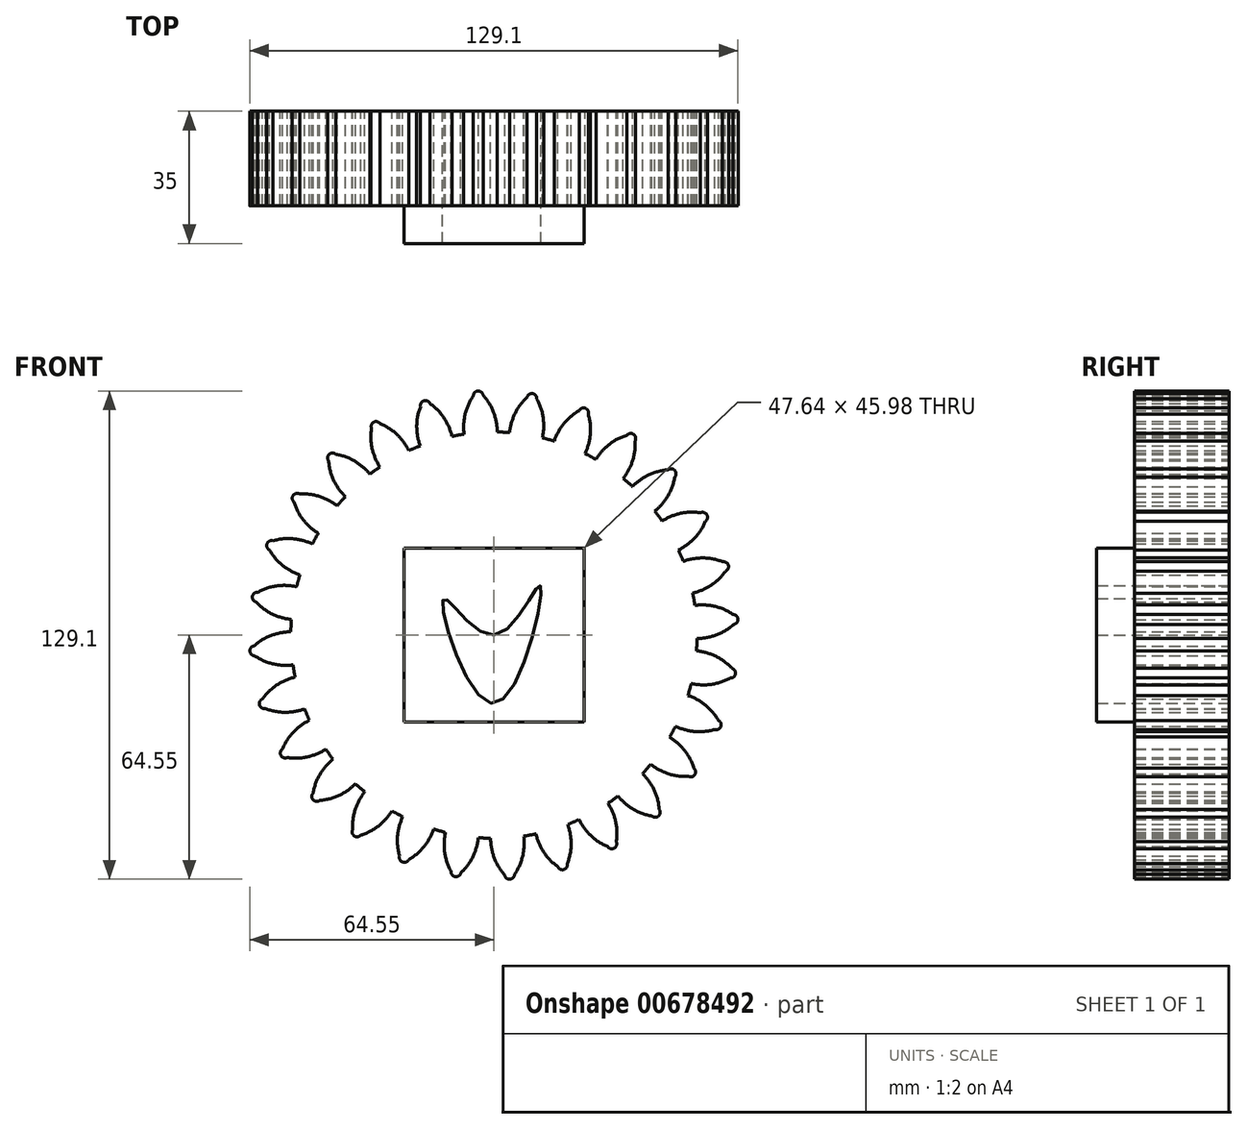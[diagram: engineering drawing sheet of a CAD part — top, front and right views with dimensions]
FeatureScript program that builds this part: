
annotation { "Feature Type Name" : "Feature", "Feature Type Description" : "" }
export const myFeature = defineFeature(function(context is Context, id is Id, definition is map)
    precondition{}
    {
        {
            var Q0;
            Q0=qCreatedBy(makeId("Front.planeOp"),FACE);
            var sketch = newSketch(context, id + "F0", { "sketchPlane" : qUnion([Q0])});
            skCircle(sketch, "E0", {"center": v(0, 0) * mm, "radius": 53.72 * mm});
            skCircle(sketch, "E1", {"center": v(0, 0) * mm, "radius": 58.67 * mm, "construction": true});
            skCircle(sketch, "E2", {"center": v(0, 0) * mm, "radius": 63.5 * mm, "construction": true});
            skLineSegment(sketch, "E3", {"start": v(0, 0) * mm, "end": v(0, 72.67) * mm, "construction": true});
            skLineSegment(sketch, "E4", {"start": v(0, 0) * mm, "end": v(-5.05, 77.02) * mm, "construction": true});
            skLineSegment(sketch, "E5", {"start": v(0, 58.67) * mm, "end": v(-57.47, 58.67) * mm, "construction": true});
            skLineSegment(sketch, "E6", {"start": v(0, 58.67) * mm, "end": v(-61.26, 36.38) * mm, "construction": true});
            skCircle(sketch, "E7", {"center": v(0, 0) * mm, "radius": 55.14 * mm, "construction": true});
            skCircle(sketch, "E8", {"center": v(0, 58.67) * mm, "radius": 14.6 * mm, "construction": true});
            skCircle(sketch, "E9", {"center": v(-13.72, 53.68) * mm, "radius": 14.6 * mm, "construction": true});
            skArc(sketch, "E10", {"start": v(0, 58.67) * mm, "mid": v(-1.19, 61.2) * mm, "end": v(-2.86, 63.44) * mm});
            skArc(sketch, "E11", {"start": v(0.88, 53.71) * mm, "mid": v(0.64, 56.23) * mm, "end": v(0, 58.67) * mm});
            skArc(sketch, "E12.MirrorCS", {"start": v(-7.66, 58.17) * mm, "mid": v(-6.8, 60.83) * mm, "end": v(-5.45, 63.27) * mm});
            skArc(sketch, "E13.MirrorCS", {"start": v(-7.88, 53.14) * mm, "mid": v(-7.98, 55.66) * mm, "end": v(-7.66, 58.17) * mm});
            skArc(sketch, "E14", {"start": v(-2.86, 63.44) * mm, "mid": v(-4.23, 64.55) * mm, "end": v(-5.45, 63.27) * mm});
            skLineSegment(sketch, "E15.bottom", {"start": v(-23.82, 23) * mm, "end": v(23.82, 23) * mm});
            skLineSegment(sketch, "E15.top", {"start": v(-23.82, -23) * mm, "end": v(23.82, -23) * mm});
            skLineSegment(sketch, "E15.left", {"start": v(-23.82, 23) * mm, "end": v(-23.82, -23) * mm});
            skLineSegment(sketch, "E15.right", {"start": v(23.82, 23) * mm, "end": v(23.82, -23) * mm});
            skFitSpline(sketch, "E16", {"points": [v(0, 0) * mm, v(12.25, 13.08) * mm, v(0, -18.04) * mm, v(-13.35, 9.5) * mm, v(0, 0) * mm]});
            skSolve(sketch);
        }
        {
            var Q0;
            {var subQ0=sQuery(id+"F0.wireOp",EDGE,"E0");var subQ1=makeQuery(id+"F0.imprint","INTERSECT",VERTEX,{"derivedFrom":[subQ0,sQuery(id+"F0.wireOp",EDGE,"E11")]});Q0=makeQuery(id+"F0.imprint","IMPRINT",FACE,{"disambiguationData":[TD([[makeQuery(id+"F0.imprint","IMPRINT",EDGE,{"disambiguationData":[TD([[subQ1,-1.0]])],"derivedFrom":subQ0}),1.0]])]});}
            var Q1;
            Q1=makeQuery(id+"F0.imprint","IMPRINT",FACE,{"disambiguationData":[TD([[makeQuery(id+"F0.imprint","IMPRINT",EDGE,{"derivedFrom":sQuery(id+"F0.wireOp",EDGE,"E10")}),1.0]])]});
            extrude(context, id + "F1", {"entities" : qUnion([Q0, Q1]), "depth" : 25 * mm, "offsetDistance" : 25 * mm});
        }
        {
            var Q0;
            Q0=makeQuery(id+"F1.opExtrude","SWEPT_BODY",BODY,{"disambiguationData":[OSD([sQuery(id+"F0.wireOp",EDGE,"E0"),sQuery(id+"F0.wireOp",EDGE,"E10"),sQuery(id+"F0.wireOp",EDGE,"E11"),sQuery(id+"F0.wireOp",EDGE,"E12.MirrorCS"),sQuery(id+"F0.wireOp",EDGE,"E13.MirrorCS"),sQuery(id+"F0.wireOp",EDGE,"E14")])]});
            var Q1;
            Q1=makeQuery(id+"F1.opExtrude","SWEPT_FACE",FACE,{"disambiguationData":[OSD([sQuery(id+"F0.wireOp",EDGE,"E0")])]});
            circularPattern(context, id + "F2", {"entities" : qUnion([Q0]), "axis" : qUnion([Q1]), "angle" : 360 * degree, "instanceCount" : 28, "equalSpace" : true});
        }
        {
            var Q0;
            Q0=makeQuery(id+"F0.imprint","IMPRINT",FACE,{"disambiguationData":[TD([[makeQuery(id+"F0.imprint","IMPRINT",EDGE,{"derivedFrom":sQuery(id+"F0.wireOp",EDGE,"E15.bottom")}),-1.0]])]});
            extrude(context, id + "F3", {"entities" : qUnion([Q0]), "operationType" : NewBodyOperationType.ADD, "depth" : 35 * mm, "offsetDistance" : 25 * mm});
        }
    });
